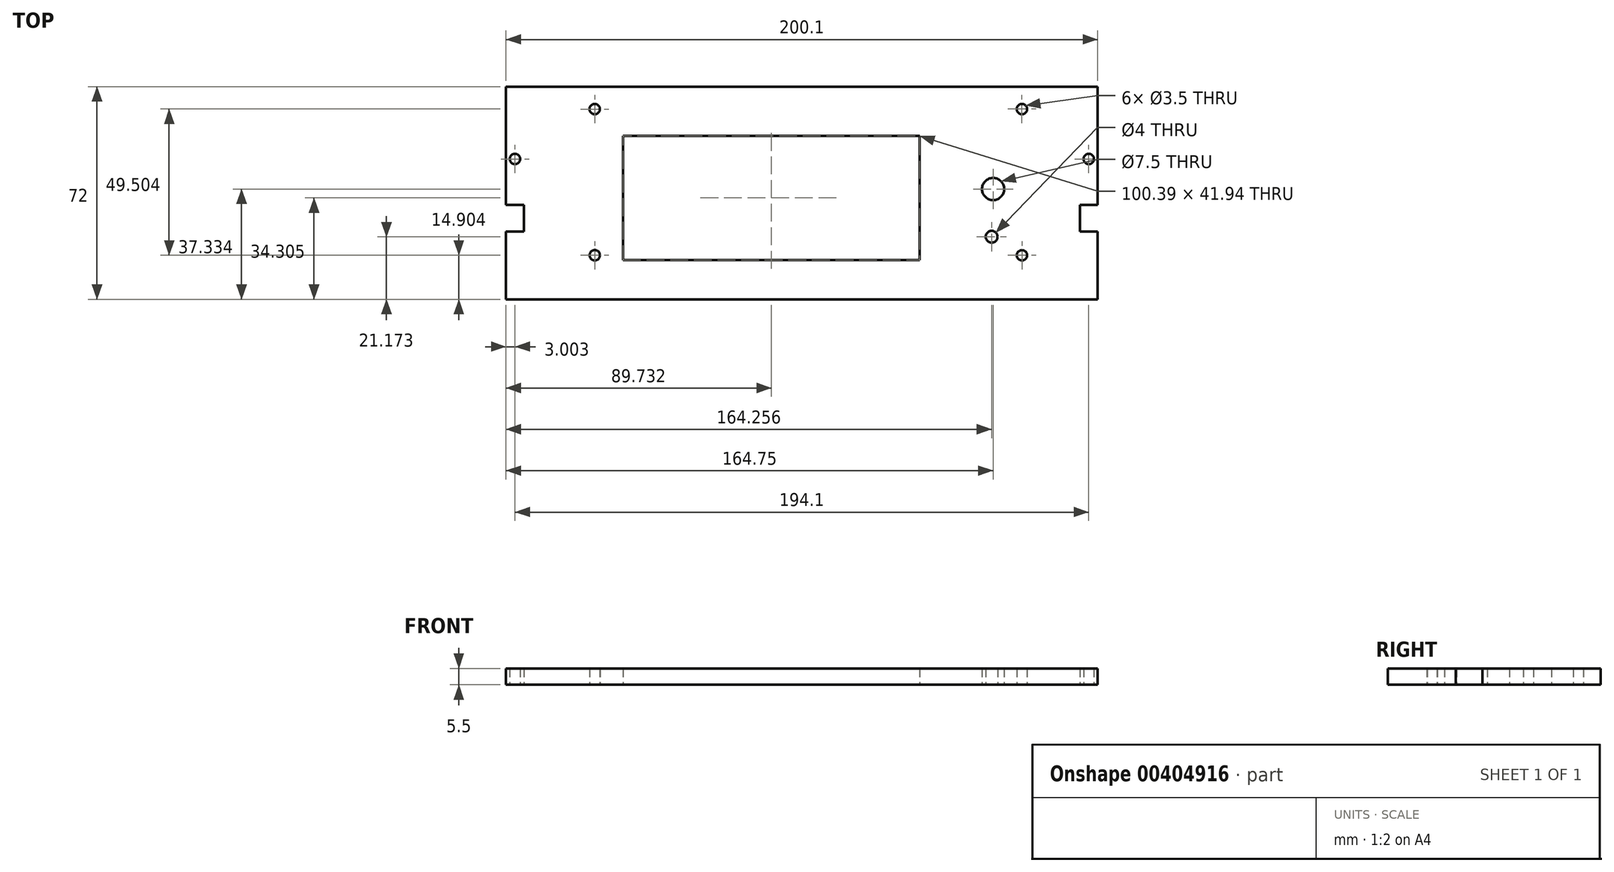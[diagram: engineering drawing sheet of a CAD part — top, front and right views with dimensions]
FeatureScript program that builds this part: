
annotation { "Feature Type Name" : "Feature", "Feature Type Description" : "" }
export const myFeature = defineFeature(function(context is Context, id is Id, definition is map)
    precondition{}
    {
        {
            var Q0;
            Q0=qCreatedBy(makeId("Top.planeOp"),FACE);
            var sketch = newSketch(context, id + "F0", { "sketchPlane" : qUnion([Q0])});
            skLineSegment(sketch, "E0.bottom", {"start": v(-102.6, 35.8) * mm, "end": v(97.5, 35.8) * mm});
            skLineSegment(sketch, "E0.top", {"start": v(-102.6, -36.2) * mm, "end": v(97.5, -36.2) * mm});
            skLineSegment(sketch, "E0.left", {"start": v(-102.6, 35.8) * mm, "end": v(-102.6, -36.2) * mm});
            skLineSegment(sketch, "E0.right", {"start": v(97.5, 35.8) * mm, "end": v(97.5, -36.2) * mm});
            skLineSegment(sketch, "E1.bottom", {"start": v(-63.06, 19.08) * mm, "end": v(37.33, 19.08) * mm});
            skLineSegment(sketch, "E1.top", {"start": v(-63.06, -22.85) * mm, "end": v(37.33, -22.85) * mm});
            skLineSegment(sketch, "E1.left", {"start": v(-63.06, 19.08) * mm, "end": v(-63.06, -22.85) * mm});
            skLineSegment(sketch, "E1.right", {"start": v(37.33, 19.08) * mm, "end": v(37.33, -22.85) * mm});
            skCircle(sketch, "E2", {"center": v(62.15, 1.14) * mm, "radius": 3.75 * mm});
            skCircle(sketch, "E3", {"center": v(61.66, -15.02) * mm, "radius": 2 * mm});
            skCircle(sketch, "E4", {"center": v(-72.6, 28.21) * mm, "radius": 1.75 * mm});
            skCircle(sketch, "E5", {"center": v(-72.6, -21.27) * mm, "radius": 1.75 * mm});
            skCircle(sketch, "E6", {"center": v(71.92, -21.29) * mm, "radius": 1.75 * mm});
            skCircle(sketch, "E7", {"center": v(71.9, 28.22) * mm, "radius": 1.75 * mm});
            skLineSegment(sketch, "E8.bottom", {"start": v(-102.6, -4.2) * mm, "end": v(-96.6, -4.2) * mm});
            skLineSegment(sketch, "E8.top", {"start": v(-102.6, -13.2) * mm, "end": v(-96.6, -13.2) * mm});
            skLineSegment(sketch, "E8.left", {"start": v(-102.6, -4.2) * mm, "end": v(-102.6, -13.2) * mm});
            skLineSegment(sketch, "E8.right", {"start": v(-96.6, -4.2) * mm, "end": v(-96.6, -13.2) * mm});
            skLineSegment(sketch, "E9.bottom", {"start": v(91.5, -4.2) * mm, "end": v(97.5, -4.2) * mm});
            skLineSegment(sketch, "E9.top", {"start": v(91.5, -13.2) * mm, "end": v(97.5, -13.2) * mm});
            skLineSegment(sketch, "E9.left", {"start": v(91.5, -4.2) * mm, "end": v(91.5, -13.2) * mm});
            skLineSegment(sketch, "E9.right", {"start": v(97.5, -4.2) * mm, "end": v(97.5, -13.2) * mm});
            skCircle(sketch, "E10", {"center": v(-99.6, 11.3) * mm, "radius": 1.75 * mm});
            skLineSegment(sketch, "E11", {"start": v(-99.6, -4.2) * mm, "end": v(-99.6, 20.1) * mm, "construction": true});
            skLineSegment(sketch, "E12", {"start": v(94.5, -4.2) * mm, "end": v(94.5, 26.8) * mm, "construction": true});
            skCircle(sketch, "E13", {"center": v(94.5, 11.3) * mm, "radius": 1.75 * mm, "construction": true});
            skCircle(sketch, "E14", {"center": v(94.5, 11.3) * mm, "radius": 1.75 * mm});
            skSolve(sketch);
        }
        {
            var Q0;
            {var subQ7=sQuery(id+"F0.wireOp",EDGE,"E0.bottom");Q0=makeQuery(id+"F0.imprint","IMPRINT",FACE,{"disambiguationData":[TD([[makeQuery(id+"F0.imprint","IMPRINT",EDGE,{"derivedFrom":subQ7}),-1.0]])]});}
            extrude(context, id + "F1", {"entities" : qUnion([Q0]), "depth" : 5.5 * mm});
        }
    });
